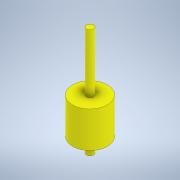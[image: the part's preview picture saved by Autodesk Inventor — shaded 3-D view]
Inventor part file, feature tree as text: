
AUTODESK INVENTOR PART (.ipt)
format: ipt  version: 2020.2 (Build 242310000, 310)  size: 105,984 bytes
history: native  units: mm
features: extrude x2, sketch x2
ambient origin geometry x8: Origin, YZ Plane, XZ Plane, XY Plane, X Axis, Y Axis, Z Axis, Center Point
bodies: Solido1 (feature_tree)
feature tree (4):
  extrude  "Estrusione1"  Depth=29.0mm
  extrude  "Estrusione2"  Depth=30.0mm TaperAngle=0.0deg
  sketch  "Schizzo1"
  sketch  "Schizzo2"
